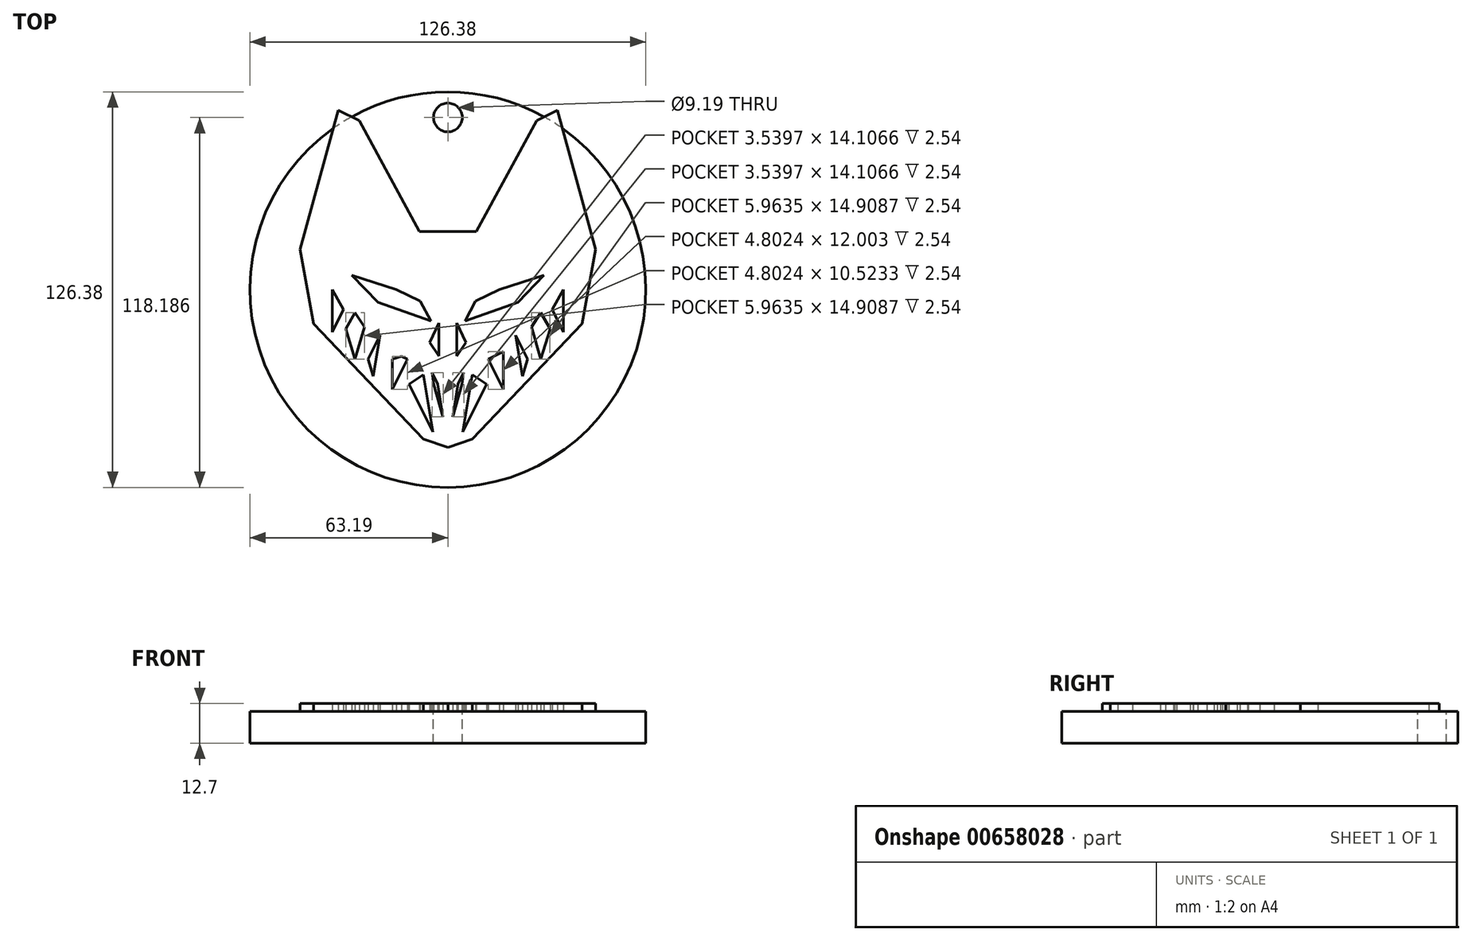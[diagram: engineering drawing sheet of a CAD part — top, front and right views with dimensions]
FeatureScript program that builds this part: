
annotation { "Feature Type Name" : "Feature", "Feature Type Description" : "" }
export const myFeature = defineFeature(function(context is Context, id is Id, definition is map)
    precondition{}
    {
        {
            var Q0;
            Q0=qCreatedBy(makeId("Top.planeOp"),FACE);
            var sketch = newSketch(context, id + "F0", { "sketchPlane" : qUnion([Q0])});
            skLineSegment(sketch, "E0", {"start": v(0, 18.55) * mm, "end": v(-9.11, 18.55) * mm});
            skLineSegment(sketch, "E1", {"start": v(-9.11, 18.55) * mm, "end": v(-28.33, 54) * mm});
            skLineSegment(sketch, "E2", {"start": v(-28.33, 54) * mm, "end": v(-34.95, 57.32) * mm});
            skLineSegment(sketch, "E3", {"start": v(-34.95, 57.32) * mm, "end": v(-47.21, 12.92) * mm});
            skLineSegment(sketch, "E4", {"start": v(-47.21, 12.92) * mm, "end": v(-42.9, -10.93) * mm});
            skLineSegment(sketch, "E5", {"start": v(-42.9, -10.93) * mm, "end": v(-7.79, -47.7) * mm});
            skLineSegment(sketch, "E6", {"start": v(-7.79, -47.7) * mm, "end": v(0, -50.36) * mm});
            skLineSegment(sketch, "E7.MirrorCS", {"start": v(0, 18.55) * mm, "end": v(9.11, 18.55) * mm});
            skLineSegment(sketch, "E8.MirrorCS", {"start": v(9.11, 18.55) * mm, "end": v(28.33, 54) * mm});
            skLineSegment(sketch, "E9.MirrorCS", {"start": v(28.33, 54) * mm, "end": v(34.95, 57.32) * mm});
            skLineSegment(sketch, "E10.MirrorCS", {"start": v(34.95, 57.32) * mm, "end": v(47.21, 12.92) * mm});
            skLineSegment(sketch, "E11.MirrorCS", {"start": v(47.21, 12.92) * mm, "end": v(42.9, -10.93) * mm});
            skLineSegment(sketch, "E12.MirrorCS", {"start": v(42.9, -10.93) * mm, "end": v(7.79, -47.7) * mm});
            skLineSegment(sketch, "E13.MirrorCS", {"start": v(7.79, -47.7) * mm, "end": v(0, -50.36) * mm});
            skSolve(sketch);
        }
        {
            var Q0;
            Q0=makeQuery(id+"F0.imprint","IMPRINT",FACE,{"disambiguationData":[TD([[makeQuery(id+"F0.imprint","IMPRINT",EDGE,{"derivedFrom":sQuery(id+"F0.wireOp",EDGE,"E0")}),1.0]])]});
            extrude(context, id + "F1", {"entities" : qUnion([Q0]), "depth" : 2.54 * mm, "offsetDistance" : 25.4 * mm});
        }
        {
            var Q0;
            Q0=qCreatedBy(makeId("Top.planeOp"),FACE);
            var sketch = newSketch(context, id + "F2", { "sketchPlane" : qUnion([Q0])});
            skLineSegment(sketch, "E14", {"start": v(-8.78, -3.64) * mm, "end": v(-16.4, 0) * mm});
            skLineSegment(sketch, "E15", {"start": v(-16.4, 0) * mm, "end": v(-30.65, 4.64) * mm});
            skLineSegment(sketch, "E16", {"start": v(-30.65, 4.64) * mm, "end": v(-22.36, -3.98) * mm});
            skLineSegment(sketch, "E17", {"start": v(-22.36, -3.98) * mm, "end": v(-5.47, -9.94) * mm});
            skLineSegment(sketch, "E18", {"start": v(-5.47, -9.94) * mm, "end": v(-8.78, -3.64) * mm});
            skLineSegment(sketch, "E19.MirrorCS", {"start": v(5.47, -9.94) * mm, "end": v(8.78, -3.64) * mm});
            skLineSegment(sketch, "E20.MirrorCS", {"start": v(22.36, -3.98) * mm, "end": v(5.47, -9.94) * mm});
            skLineSegment(sketch, "E21.MirrorCS", {"start": v(8.78, -3.64) * mm, "end": v(16.4, 0) * mm});
            skLineSegment(sketch, "E22.MirrorCS", {"start": v(16.4, 0) * mm, "end": v(30.65, 4.64) * mm});
            skLineSegment(sketch, "E23.MirrorCS", {"start": v(30.65, 4.64) * mm, "end": v(22.36, -3.98) * mm});
            skSolve(sketch);
        }
        {
            var Q0;
            Q0 = qSketchRegion(id + "F2", true);
            extrude(context, id + "F3", {"entities" : qUnion([Q0]), "operationType" : NewBodyOperationType.REMOVE, "depth" : 86.1 * mm, "offsetDistance" : 25.4 * mm});
        }
        {
            var Q0;
            Q0=qCreatedBy(makeId("Top.planeOp"),FACE);
            var sketch = newSketch(context, id + "F4", { "sketchPlane" : qUnion([Q0])});
            skLineSegment(sketch, "E24", {"start": v(-33.3, -6.3) * mm, "end": v(-36.94, 0) * mm});
            skLineSegment(sketch, "E25", {"start": v(-36.94, 0) * mm, "end": v(-36.94, -5.63) * mm});
            skLineSegment(sketch, "E26", {"start": v(-36.94, -5.63) * mm, "end": v(-36.94, -13.58) * mm});
            skLineSegment(sketch, "E27", {"start": v(-36.94, -13.58) * mm, "end": v(-33.3, -6.3) * mm});
            skLineSegment(sketch, "E28", {"start": v(-26.67, -11.93) * mm, "end": v(-29.65, -7.29) * mm});
            skLineSegment(sketch, "E29", {"start": v(-29.65, -7.29) * mm, "end": v(-32.63, -12.59) * mm});
            skLineSegment(sketch, "E30", {"start": v(-32.63, -12.59) * mm, "end": v(-29.65, -22.2) * mm});
            skLineSegment(sketch, "E31", {"start": v(-29.65, -22.2) * mm, "end": v(-26.67, -11.93) * mm});
            skLineSegment(sketch, "E32", {"start": v(-21.7, -14.58) * mm, "end": v(-25.51, -22.2) * mm});
            skLineSegment(sketch, "E33", {"start": v(-25.51, -22.2) * mm, "end": v(-23.83, -27.62) * mm});
            skLineSegment(sketch, "E34", {"start": v(-23.83, -27.62) * mm, "end": v(-21.7, -14.58) * mm});
            skLineSegment(sketch, "E35", {"start": v(-17.72, -22.2) * mm, "end": v(-14.77, -21.28) * mm});
            skLineSegment(sketch, "E36", {"start": v(-14.77, -21.28) * mm, "end": v(-12.93, -22.2) * mm});
            skLineSegment(sketch, "E37", {"start": v(-12.93, -22.2) * mm, "end": v(-17.73, -31.8) * mm});
            skLineSegment(sketch, "E38", {"start": v(-17.73, -31.8) * mm, "end": v(-17.72, -22.2) * mm});
            skLineSegment(sketch, "E39", {"start": v(-12.42, -30.15) * mm, "end": v(-7.79, -27.17) * mm});
            skLineSegment(sketch, "E40", {"start": v(-7.79, -27.17) * mm, "end": v(-4.8, -45.39) * mm});
            skLineSegment(sketch, "E41", {"start": v(-4.8, -45.39) * mm, "end": v(-12.42, -30.15) * mm});
            skLineSegment(sketch, "E42.MirrorCS", {"start": v(7.79, -27.17) * mm, "end": v(4.8, -45.39) * mm});
            skLineSegment(sketch, "E43.MirrorCS", {"start": v(4.8, -45.39) * mm, "end": v(12.42, -30.15) * mm});
            skLineSegment(sketch, "E44.MirrorCS", {"start": v(12.42, -30.15) * mm, "end": v(7.79, -27.17) * mm});
            skLineSegment(sketch, "E45.MirrorCS", {"start": v(12.93, -22.2) * mm, "end": v(17.73, -31.8) * mm});
            skLineSegment(sketch, "E46.MirrorCS", {"start": v(17.73, -31.8) * mm, "end": v(17.72, -22.2) * mm});
            skLineSegment(sketch, "E47.MirrorCS", {"start": v(23.83, -27.62) * mm, "end": v(21.7, -14.58) * mm});
            skLineSegment(sketch, "E48.MirrorCS", {"start": v(21.7, -14.58) * mm, "end": v(25.51, -22.2) * mm});
            skLineSegment(sketch, "E49.MirrorCS", {"start": v(29.65, -22.2) * mm, "end": v(26.67, -11.93) * mm});
            skLineSegment(sketch, "E50.MirrorCS", {"start": v(32.63, -12.59) * mm, "end": v(29.65, -22.2) * mm});
            skLineSegment(sketch, "E51.MirrorCS", {"start": v(29.65, -7.29) * mm, "end": v(32.63, -12.59) * mm});
            skLineSegment(sketch, "E52.MirrorCS", {"start": v(36.94, -13.58) * mm, "end": v(33.3, -6.3) * mm});
            skLineSegment(sketch, "E53.MirrorCS", {"start": v(33.3, -6.3) * mm, "end": v(36.94, 0) * mm});
            skLineSegment(sketch, "E54.MirrorCS", {"start": v(36.94, -5.63) * mm, "end": v(36.94, -13.58) * mm});
            skLineSegment(sketch, "E55", {"start": v(36.94, 0) * mm, "end": v(36.94, -5.63) * mm});
            skLineSegment(sketch, "E56", {"start": v(26.67, -11.93) * mm, "end": v(29.65, -7.29) * mm});
            skLineSegment(sketch, "E57", {"start": v(25.51, -22.2) * mm, "end": v(23.83, -27.62) * mm});
            skLineSegment(sketch, "E58", {"start": v(12.93, -22.2) * mm, "end": v(17.72, -19.8) * mm});
            skLineSegment(sketch, "E59", {"start": v(-4.47, -30.15) * mm, "end": v(-5.07, -26.49) * mm});
            skLineSegment(sketch, "E60", {"start": v(-5.07, -26.49) * mm, "end": v(-3.24, -30.15) * mm});
            skLineSegment(sketch, "E61", {"start": v(-3.24, -30.15) * mm, "end": v(-1.53, -40.6) * mm});
            skLineSegment(sketch, "E62", {"start": v(-1.53, -40.6) * mm, "end": v(-4.47, -30.15) * mm});
            skLineSegment(sketch, "E63.MirrorCS", {"start": v(1.53, -40.6) * mm, "end": v(4.47, -30.15) * mm});
            skLineSegment(sketch, "E64.MirrorCS", {"start": v(3.24, -30.15) * mm, "end": v(1.53, -40.6) * mm});
            skLineSegment(sketch, "E65.MirrorCS", {"start": v(5.07, -26.49) * mm, "end": v(3.24, -30.15) * mm});
            skLineSegment(sketch, "E66", {"start": v(5.07, -26.49) * mm, "end": v(4.47, -30.15) * mm});
            skLineSegment(sketch, "E67", {"start": v(17.72, -22.2) * mm, "end": v(17.72, -19.8) * mm});
            skSolve(sketch);
        }
        {
            var Q0;
            Q0 = qSketchRegion(id + "F4", true);
            extrude(context, id + "F5", {"entities" : qUnion([Q0]), "operationType" : NewBodyOperationType.REMOVE, "depth" : 95.25 * mm, "offsetDistance" : 25.4 * mm});
        }
        {
            var Q0;
            Q0=qCreatedBy(makeId("Top.planeOp"),FACE);
            var sketch = newSketch(context, id + "F6", { "sketchPlane" : qUnion([Q0])});
            skLineSegment(sketch, "E68", {"start": v(-2.82, -10.6) * mm, "end": v(-5.8, -16.9) * mm});
            skLineSegment(sketch, "E69", {"start": v(-5.8, -16.9) * mm, "end": v(-2.82, -21.2) * mm});
            skLineSegment(sketch, "E70", {"start": v(-2.82, -21.2) * mm, "end": v(-2.82, -10.6) * mm});
            skLineSegment(sketch, "E71.MirrorCS", {"start": v(2.82, -21.2) * mm, "end": v(2.82, -10.6) * mm});
            skLineSegment(sketch, "E72.MirrorCS", {"start": v(5.8, -16.9) * mm, "end": v(2.82, -21.2) * mm});
            skLineSegment(sketch, "E73.MirrorCS", {"start": v(2.82, -10.6) * mm, "end": v(5.8, -16.9) * mm});
            skSolve(sketch);
        }
        {
            var Q0;
            Q0 = qSketchRegion(id + "F6", true);
            extrude(context, id + "F7", {"entities" : qUnion([Q0]), "operationType" : NewBodyOperationType.REMOVE, "depth" : 55.63 * mm, "offsetDistance" : 25.4 * mm});
        }
        {
            var Q0;
            Q0=makeQuery(id+"F1.opExtrude","CAP_FACE",FACE,{"disambiguationData":[OSD([sQuery(id+"F0.wireOp",EDGE,"E0"),sQuery(id+"F0.wireOp",EDGE,"E1"),sQuery(id+"F0.wireOp",EDGE,"E2"),sQuery(id+"F0.wireOp",EDGE,"E3"),sQuery(id+"F0.wireOp",EDGE,"E4"),sQuery(id+"F0.wireOp",EDGE,"E5"),sQuery(id+"F0.wireOp",EDGE,"E6"),sQuery(id+"F0.wireOp",EDGE,"E7.MirrorCS"),sQuery(id+"F0.wireOp",EDGE,"E8.MirrorCS"),sQuery(id+"F0.wireOp",EDGE,"E9.MirrorCS"),sQuery(id+"F0.wireOp",EDGE,"E10.MirrorCS"),sQuery(id+"F0.wireOp",EDGE,"E11.MirrorCS"),sQuery(id+"F0.wireOp",EDGE,"E12.MirrorCS"),sQuery(id+"F0.wireOp",EDGE,"E13.MirrorCS")])],"isStart":true});
            var sketch = newSketch(context, id + "F8", { "sketchPlane" : qUnion([Q0])});
            skCircle(sketch, "E74", {"center": v(0, 0) * mm, "radius": 63.19 * mm});
            skSolve(sketch);
        }
        {
            var Q0;
            Q0 = qSketchRegion(id + "F8", true);
            extrude(context, id + "F9", {"entities" : qUnion([Q0]), "operationType" : NewBodyOperationType.ADD, "depth" : 2.54 * mm, "offsetDistance" : 25.4 * mm});
        }
        {
            var Q0;
            {var subQ1=sQuery(id+"F0.wireOp",EDGE,"E1");var subQ6=sQuery(id+"F8.wireOp",EDGE,"E74");Q0=makeQuery(id+"F9.boolean.opBoolean","SPLIT",FACE,{"disambiguationData":[TD([makeQuery(id+"F1.opExtrude","SWEPT_FACE",FACE,{"disambiguationData":[OSD([subQ1])]})])],"derivedFrom":makeQuery(id+"F9.opExtrude","CAP_FACE",FACE,{"disambiguationData":[OSD([subQ6])],"isStart":true})});}
            var sketch = newSketch(context, id + "F10", { "sketchPlane" : qUnion([Q0])});
            skCircle(sketch, "E75", {"center": v(0, 55) * mm, "radius": 4.6 * mm});
            skSolve(sketch);
        }
        {
            var Q0;
            Q0 = qSketchRegion(id + "F10", true);
            extrude(context, id + "F11", {"entities" : qUnion([Q0]), "operationType" : NewBodyOperationType.REMOVE, "oppositeDirection" : true, "depth" : 25.4 * mm, "offsetDistance" : 25.4 * mm});
        }
        {
            var Q0;
            Q0=makeQuery(id+"F9.opExtrude","CAP_FACE",FACE,{"disambiguationData":[OSD([sQuery(id+"F8.wireOp",EDGE,"E74")])],"isStart":false});
            extrude(context, id + "F12", {"entities" : qUnion([Q0]), "operationType" : NewBodyOperationType.ADD, "depth" : 7.62 * mm, "offsetDistance" : 25.4 * mm});
        }
    });
